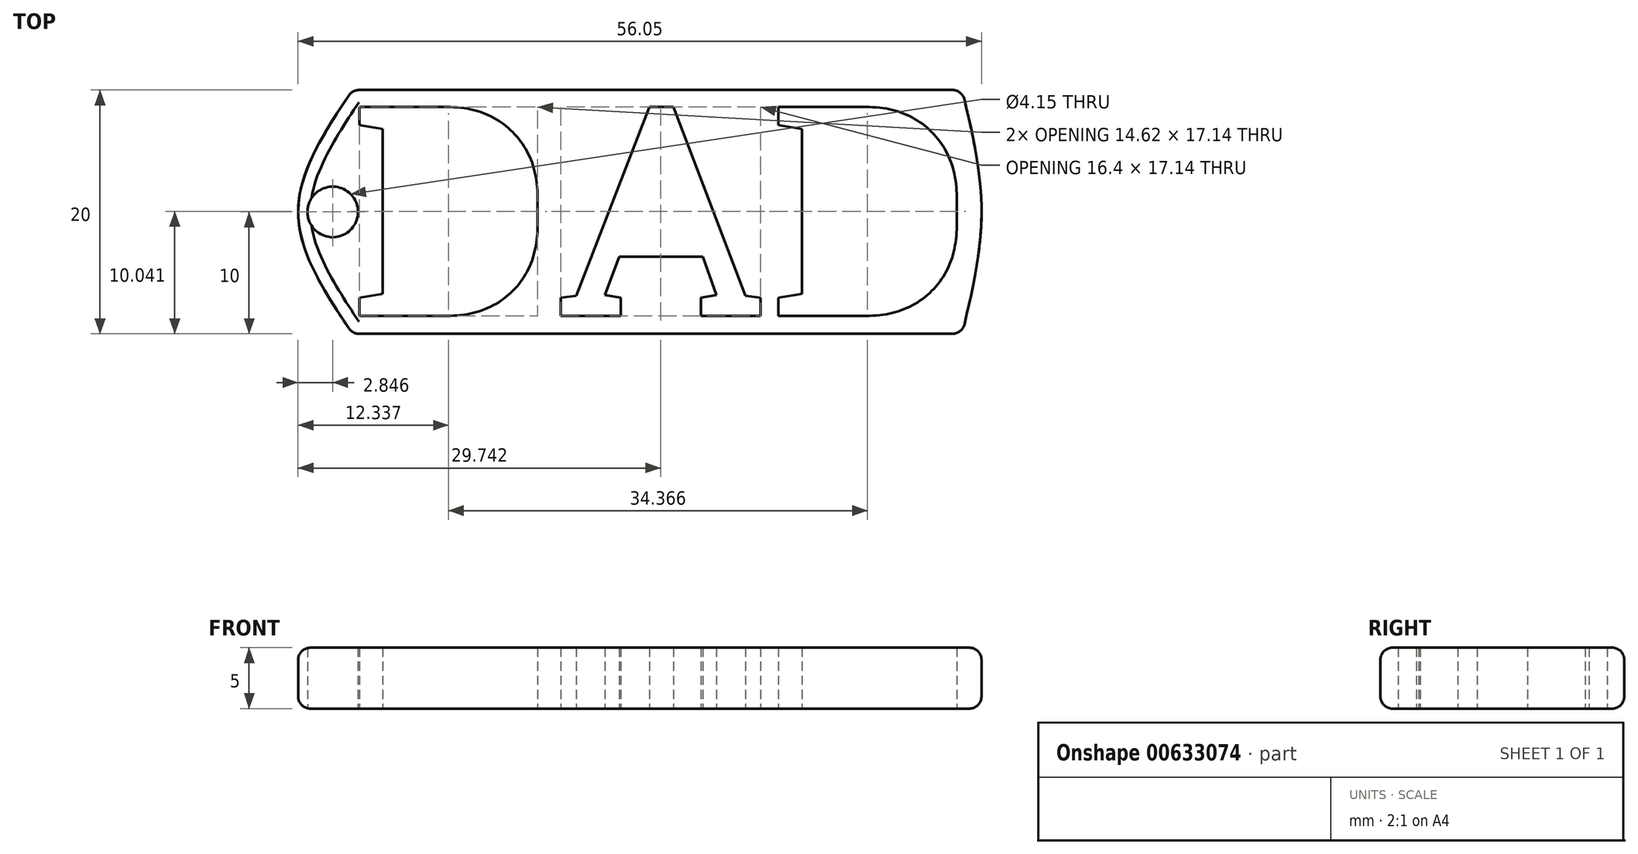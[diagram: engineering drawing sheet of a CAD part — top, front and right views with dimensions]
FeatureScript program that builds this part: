
annotation { "Feature Type Name" : "Feature", "Feature Type Description" : "" }
export const myFeature = defineFeature(function(context is Context, id is Id, definition is map)
    precondition{}
    {
        {
            var Q0;
            Q0=qCreatedBy(makeId("Top.planeOp"),FACE);
            var sketch = newSketch(context, id + "F0", { "sketchPlane" : qUnion([Q0])});
            skLineSegment(sketch, "E0.bottom", {"start": v(-25, 10) * mm, "end": v(25, 10) * mm});
            skLineSegment(sketch, "E0.top", {"start": v(-25, -10) * mm, "end": v(25, -10) * mm});
            skPoint(sketch, "E0.middle", {"position": v(0, 0) * mm});
            skText(sketch, "E1", { "text": "DAD", "fontName": "RobotoSlab-Regular.ttf"});
            skFitSpline(sketch, "E2", {"points": [v(25, 10) * mm, v(26.59, 0) * mm, v(25, -10) * mm], "startDerivative": vector(4.76, -20) * mm, "endDerivative": vector(-4.76, -20) * mm});
            skFitSpline(sketch, "E3", {"points": [v(-25, 10) * mm, v(-29.46, 0) * mm, v(-25, -10) * mm], "startDerivative": vector(-13.37, -20) * mm, "endDerivative": vector(13.37, -20) * mm});
            skCircle(sketch, "E4", {"center": v(-26.61, 0) * mm, "radius": 2.07 * mm});
            const initialGuessF0  = {"E1": [-0.02527, -0.00853, 1, 0, 0.01736]};
            skSetInitialGuess(sketch, initialGuessF0);
            skSolve(sketch);
        }
        {
            var Q0;
            Q0 = qSketchRegion(id + "F0", true);
            extrude(context, id + "F1", {"entities" : qUnion([Q0]), "depth" : 5 * mm, "offsetDistance" : 25 * mm});
        }
        {
            var Q0;
            Q0=makeQuery(id+"F1.opExtrude","CAP_EDGE",EDGE,{"disambiguationData":[OSD([sQuery(id+"F0.wireOp",EDGE,"E2")])],"isStart":false});
            var Q1;
            Q1=makeQuery(id+"F1.opExtrude","CAP_EDGE",EDGE,{"disambiguationData":[OSD([sQuery(id+"F0.wireOp",EDGE,"E0.bottom")])],"isStart":false});
            var Q2;
            Q2=makeQuery(id+"F1.opExtrude","CAP_EDGE",EDGE,{"disambiguationData":[OSD([sQuery(id+"F0.wireOp",EDGE,"E3")])],"isStart":false});
            var Q3;
            Q3=makeQuery(id+"F1.opExtrude","CAP_EDGE",EDGE,{"disambiguationData":[OSD([sQuery(id+"F0.wireOp",EDGE,"E0.top")])],"isStart":false});
            fillet(context, id + "F2", {"entities" : qUnion([Q0, Q1, Q2, Q3]), "radius" : 1 * mm, "tangentPropagation" : true, "allowEdgeOverflow" : false});
        }
        {
            var Q0;
            Q0=makeQuery(id+"F1.opExtrude","CAP_EDGE",EDGE,{"disambiguationData":[OSD([sQuery(id+"F0.wireOp",EDGE,"E2")])],"isStart":true});
            var Q1;
            Q1=makeQuery(id+"F1.opExtrude","CAP_EDGE",EDGE,{"disambiguationData":[OSD([sQuery(id+"F0.wireOp",EDGE,"E0.bottom")])],"isStart":true});
            var Q2;
            Q2=makeQuery(id+"F1.opExtrude","SWEPT_EDGE",EDGE,{"disambiguationData":[OSD([sQuery(id+"F0.wireOp",EDGE,"E0.bottom"),sQuery(id+"F0.wireOp",EDGE,"E2")])]});
            var Q3;
            Q3=makeQuery(id+"F1.opExtrude","SWEPT_EDGE",EDGE,{"disambiguationData":[OSD([sQuery(id+"F0.wireOp",EDGE,"E0.top"),sQuery(id+"F0.wireOp",EDGE,"E2")])]});
            var Q4;
            Q4=makeQuery(id+"F1.opExtrude","CAP_EDGE",EDGE,{"disambiguationData":[OSD([sQuery(id+"F0.wireOp",EDGE,"E0.top")])],"isStart":true});
            var Q5;
            Q5=makeQuery(id+"F1.opExtrude","CAP_EDGE",EDGE,{"disambiguationData":[OSD([sQuery(id+"F0.wireOp",EDGE,"E3")])],"isStart":true});
            var Q6;
            Q6=makeQuery(id+"F1.opExtrude","SWEPT_EDGE",EDGE,{"disambiguationData":[OSD([sQuery(id+"F0.wireOp",EDGE,"E0.top"),sQuery(id+"F0.wireOp",EDGE,"E3")])]});
            var Q7;
            Q7=makeQuery(id+"F1.opExtrude","SWEPT_EDGE",EDGE,{"disambiguationData":[OSD([sQuery(id+"F0.wireOp",EDGE,"E0.bottom"),sQuery(id+"F0.wireOp",EDGE,"E3")])]});
            fillet(context, id + "F3", {"entities" : qUnion([Q0, Q1, Q2, Q3, Q4, Q5, Q6, Q7]), "radius" : 1 * mm, "tangentPropagation" : true, "allowEdgeOverflow" : false});
        }
    });
